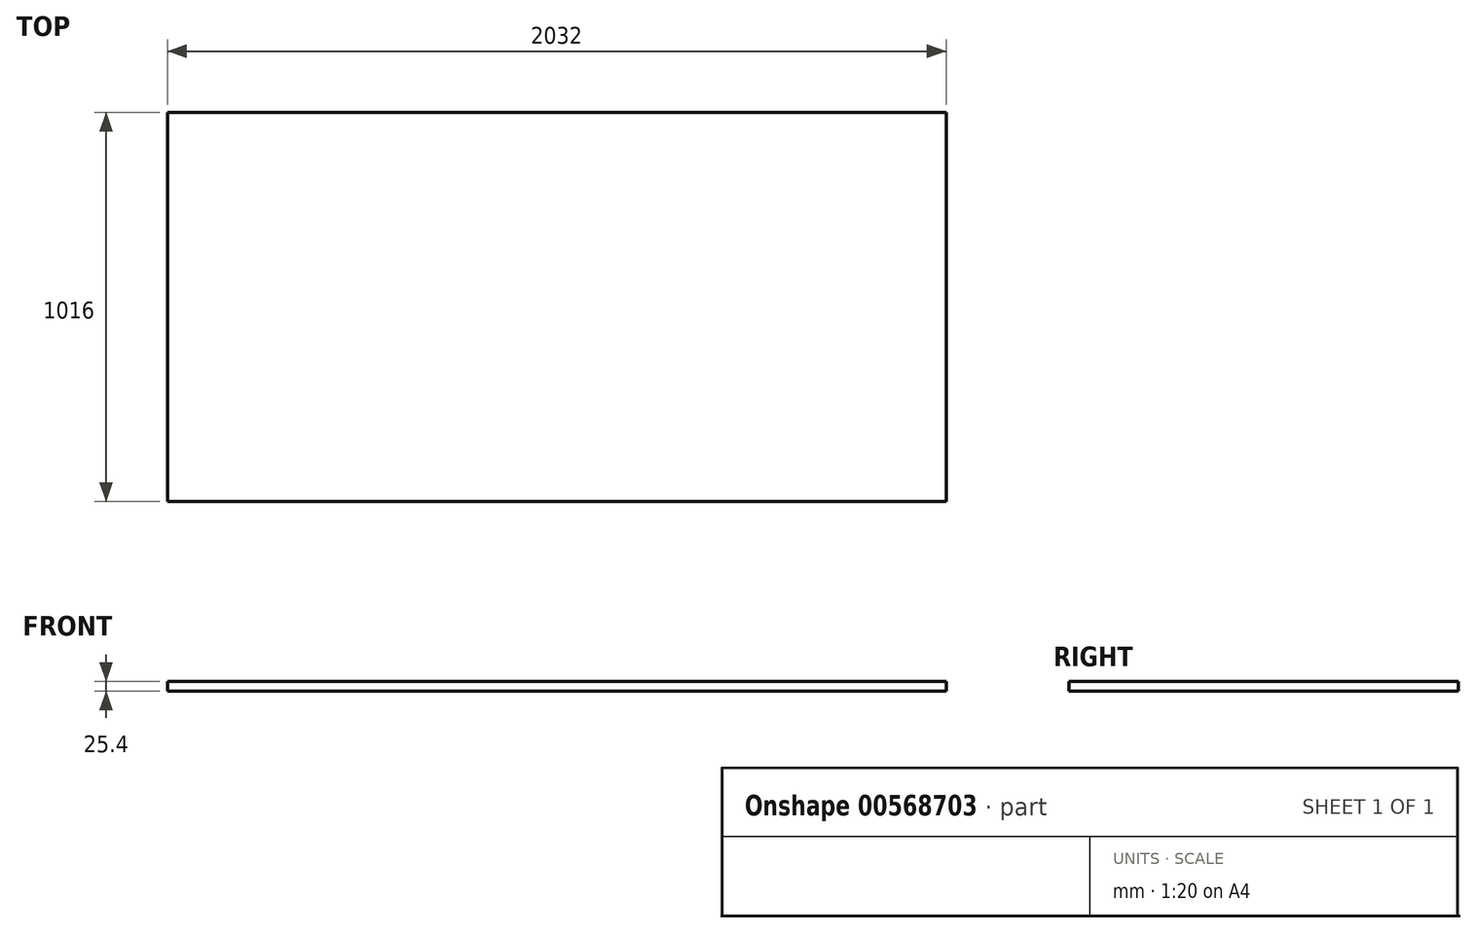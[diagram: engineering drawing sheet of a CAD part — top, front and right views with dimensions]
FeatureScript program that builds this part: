
annotation { "Feature Type Name" : "Feature", "Feature Type Description" : "" }
export const myFeature = defineFeature(function(context is Context, id is Id, definition is map)
    precondition{}
    {
        {
            var Q0;
            Q0=qCreatedBy(makeId("Front.planeOp"),FACE);
            var sketch = newSketch(context, id + "F0", { "sketchPlane" : qUnion([Q0])});
            skLineSegment(sketch, "E0.bottom", {"start": v(-1016, 12.7) * mm, "end": v(1016, 12.7) * mm});
            skLineSegment(sketch, "E0.top", {"start": v(-1016, -12.7) * mm, "end": v(1016, -12.7) * mm});
            skLineSegment(sketch, "E0.left", {"start": v(-1016, 12.7) * mm, "end": v(-1016, -12.7) * mm});
            skLineSegment(sketch, "E0.right", {"start": v(1016, 12.7) * mm, "end": v(1016, -12.7) * mm});
            skPoint(sketch, "E0.middle", {"position": v(0, 0) * mm});
            skSolve(sketch);
        }
        {
            var Q0;
            Q0 = qSketchRegion(id + "F0", true);
            extrude(context, id + "F1", {"entities" : qUnion([Q0]), "depth" : 1016 * mm, "offsetDistance" : 25.4 * mm});
        }
    });
